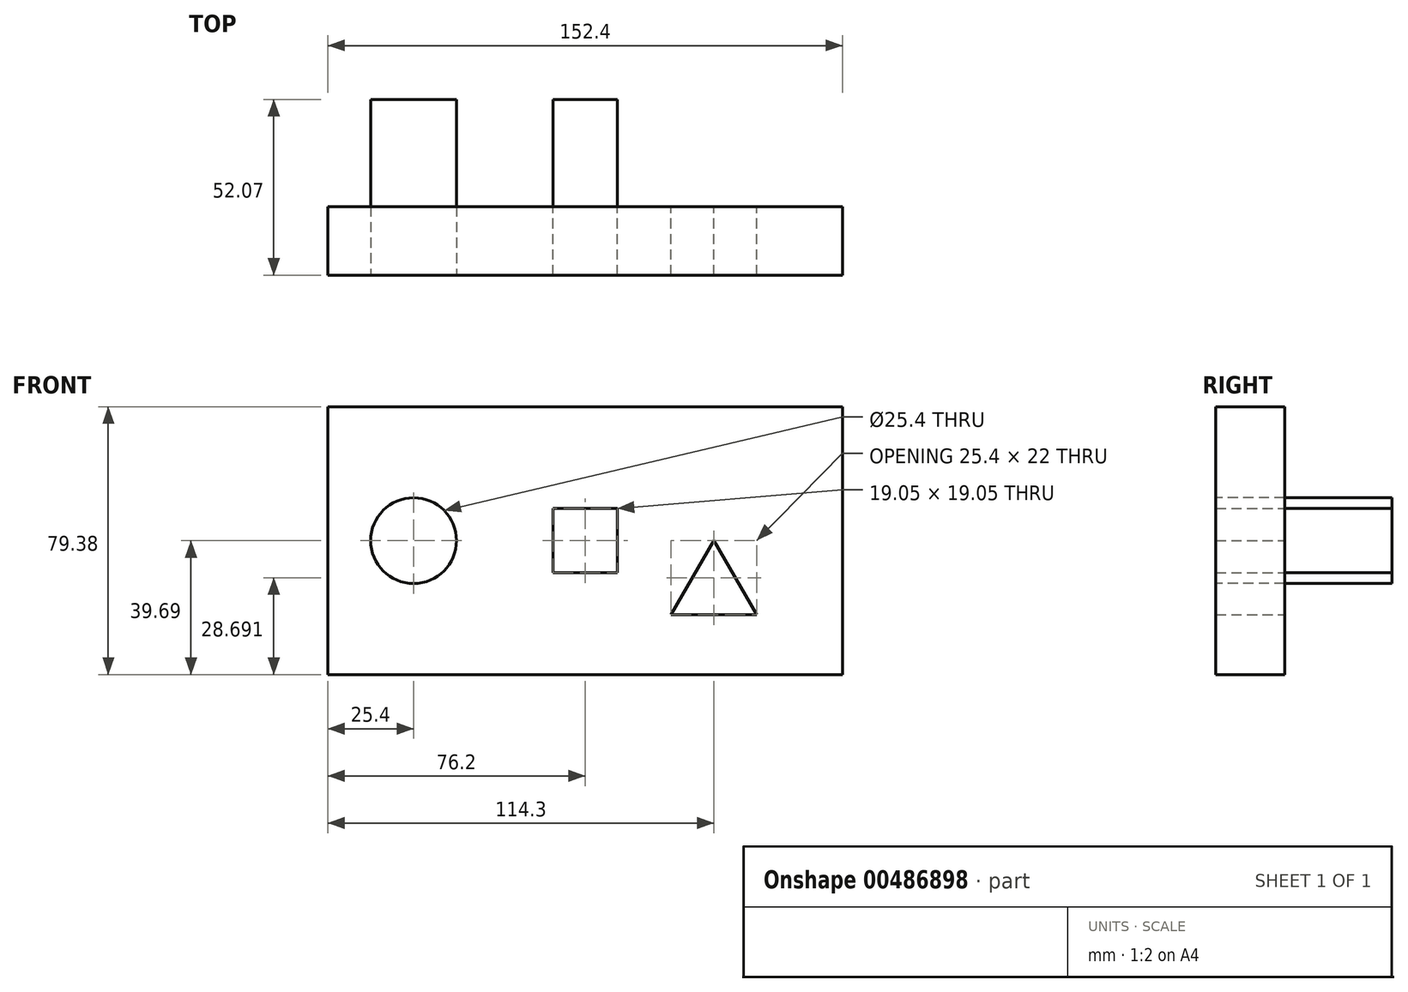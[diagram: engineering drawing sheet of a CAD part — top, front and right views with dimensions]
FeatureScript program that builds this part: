
annotation { "Feature Type Name" : "Feature", "Feature Type Description" : "" }
export const myFeature = defineFeature(function(context is Context, id is Id, definition is map)
    precondition{}
    {
        {
            var Q0;
            Q0=qCreatedBy(makeId("Front.planeOp"),FACE);
            var sketch = newSketch(context, id + "F0", { "sketchPlane" : qUnion([Q0])});
            skLineSegment(sketch, "E0", {"start": v(0, 0) * mm, "end": v(6.35, 0) * mm});
            skLineSegment(sketch, "E1", {"start": v(6.35, 0) * mm, "end": v(-6.35, -22) * mm});
            skLineSegment(sketch, "E2", {"start": v(-6.35, -22) * mm, "end": v(19.05, -22) * mm});
            skLineSegment(sketch, "E3", {"start": v(19.05, -22) * mm, "end": v(6.35, 0) * mm});
            skLineSegment(sketch, "E4", {"start": v(0, 0) * mm, "end": v(-31.75, 0) * mm});
            skLineSegment(sketch, "E5.bottom", {"start": v(-22.22, -9.53) * mm, "end": v(-41.28, -9.52) * mm});
            skLineSegment(sketch, "E5.top", {"start": v(-22.22, 9.53) * mm, "end": v(-41.27, 9.53) * mm});
            skLineSegment(sketch, "E5.left", {"start": v(-22.22, -9.53) * mm, "end": v(-22.22, 9.52) * mm});
            skLineSegment(sketch, "E5.right", {"start": v(-41.27, -9.52) * mm, "end": v(-41.27, 9.53) * mm});
            skPoint(sketch, "E5.middle", {"position": v(-31.75, 0) * mm});
            skLineSegment(sketch, "E6", {"start": v(-31.75, 0) * mm, "end": v(-82.55, 0) * mm});
            skCircle(sketch, "E7", {"center": v(-82.55, 0) * mm, "radius": 12.7 * mm});
            skLineSegment(sketch, "E8.bottom", {"start": v(-107.95, 39.69) * mm, "end": v(44.45, 39.69) * mm});
            skLineSegment(sketch, "E8.top", {"start": v(-107.95, -39.69) * mm, "end": v(44.45, -39.69) * mm});
            skLineSegment(sketch, "E8.left", {"start": v(-107.95, 39.69) * mm, "end": v(-107.95, -39.69) * mm});
            skLineSegment(sketch, "E8.right", {"start": v(44.45, 39.69) * mm, "end": v(44.45, -39.69) * mm});
            skLineSegment(sketch, "E9", {"start": v(0, 0) * mm, "end": v(0, -39.69) * mm});
            skSolve(sketch);
        }
        {
            var Q0;
            {var subQ7=sQuery(id+"F0.wireOp",EDGE,"E0");Q0=makeQuery(id+"F0.imprint","IMPRINT",FACE,{"disambiguationData":[TD([[makeQuery(id+"F0.imprint","IMPRINT",EDGE,{"derivedFrom":subQ7}),1.0]])]});}
            var Q1;
            {var subQ0=sQuery(id+"F0.wireOp",EDGE,"E0");Q1=makeQuery(id+"F0.imprint","IMPRINT",FACE,{"disambiguationData":[TD([[makeQuery(id+"F0.imprint","IMPRINT",EDGE,{"derivedFrom":subQ0}),-1.0]])]});}
            extrude(context, id + "F1", {"entities" : qUnion([Q0, Q1]), "depth" : 20.32 * mm});
        }
        {
            var Q0;
            Q0=makeQuery(id+"F0.imprint","IMPRINT",FACE,{"disambiguationData":[TD([[makeQuery(id+"F0.imprint","IMPRINT",EDGE,{"derivedFrom":sQuery(id+"F0.wireOp",EDGE,"E7")}),1.0]])]});
            extrude(context, id + "F2", {"entities" : qUnion([Q0]), "oppositeDirection" : true, "depth" : 31.75 * mm, "hasSecondDirection" : true, "secondDirectionOppositeDirection" : false, "secondDirectionDepth" : 20.32 * mm});
        }
        {
            var Q0;
            {var subQ1=sQuery(id+"F0.wireOp",EDGE,"E5.bottom");Q0=makeQuery(id+"F0.imprint","IMPRINT",FACE,{"disambiguationData":[TD([[makeQuery(id+"F0.imprint","IMPRINT",EDGE,{"derivedFrom":subQ1}),-1.0]])]});}
            var Q1;
            {var subQ1=sQuery(id+"F0.wireOp",EDGE,"E5.top");Q1=makeQuery(id+"F0.imprint","IMPRINT",FACE,{"disambiguationData":[TD([[makeQuery(id+"F0.imprint","IMPRINT",EDGE,{"derivedFrom":subQ1}),1.0]])]});}
            extrude(context, id + "F3", {"entities" : qUnion([Q0, Q1]), "oppositeDirection" : true, "depth" : 31.75 * mm});
        }
    });
